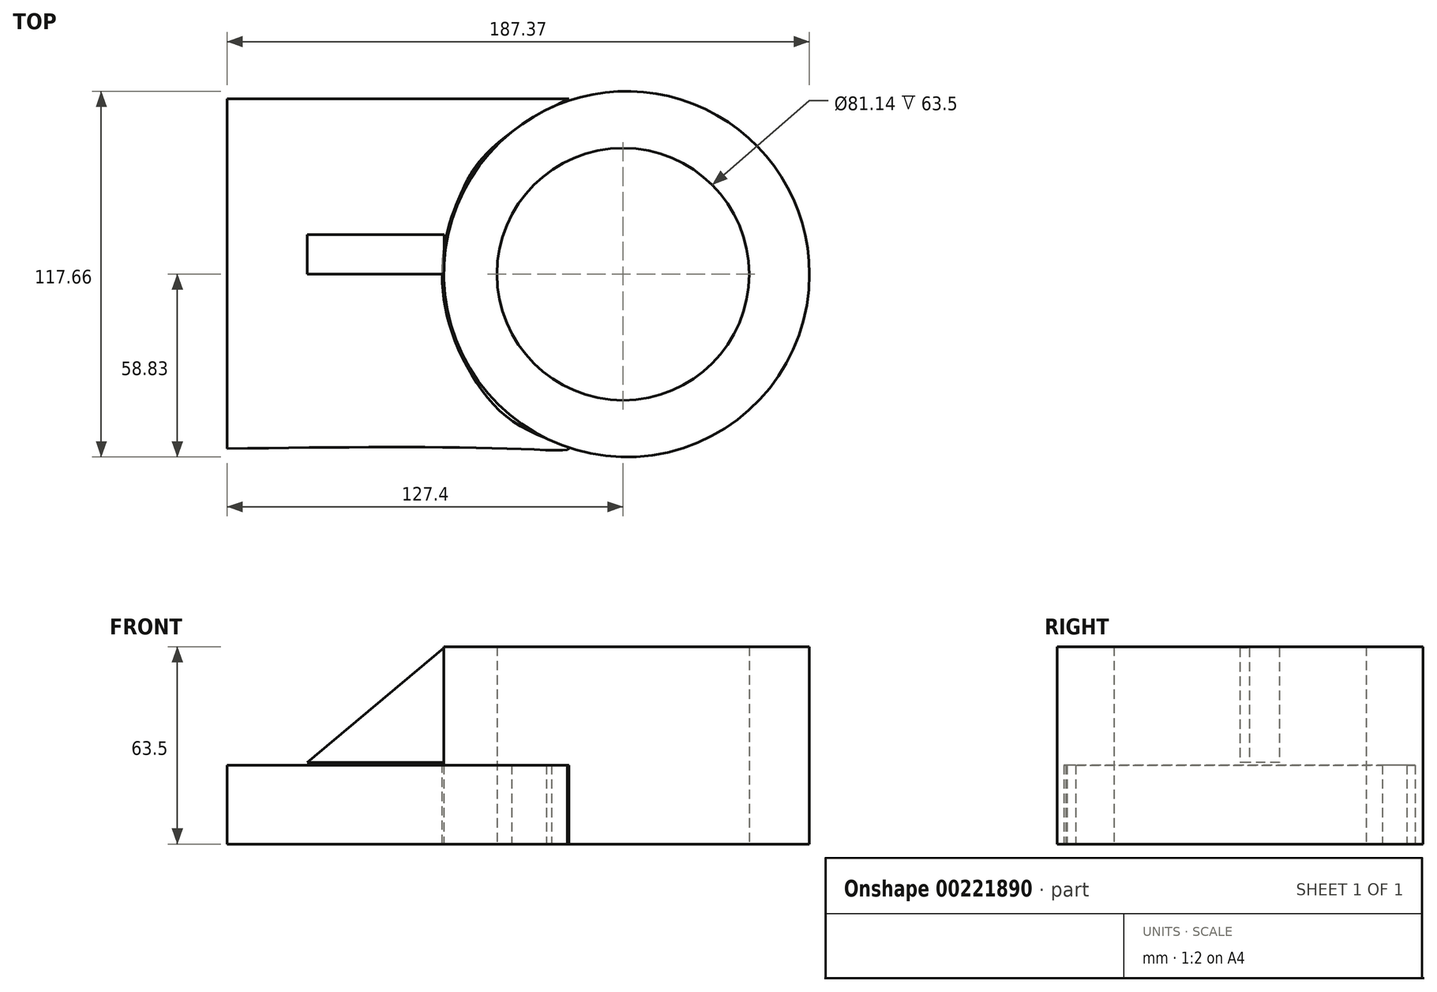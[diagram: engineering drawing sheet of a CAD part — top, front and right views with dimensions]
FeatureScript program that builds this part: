
annotation { "Feature Type Name" : "Feature", "Feature Type Description" : "" }
export const myFeature = defineFeature(function(context is Context, id is Id, definition is map)
    precondition{}
    {
        {
            var Q0;
            Q0=qCreatedBy(makeId("Top.planeOp"),FACE);
            var sketch = newSketch(context, id + "F0", { "sketchPlane" : qUnion([Q0])});
            skCircle(sketch, "E0", {"center": v(78.28, 0) * mm, "radius": 58.83 * mm});
            skSolve(sketch);
        }
        {
            var Q0;
            Q0 = qSketchRegion(id + "F0", true);
            extrude(context, id + "F1", {"entities" : qUnion([Q0]), "depth" : 63.5 * mm});
        }
        {
            var Q0;
            Q0=qCreatedBy(makeId("Top.planeOp"),FACE);
            var sketch = newSketch(context, id + "F2", { "sketchPlane" : qUnion([Q0])});
            skCircle(sketch, "E1", {"center": v(77.14, 0) * mm, "radius": 40.57 * mm});
            skSolve(sketch);
        }
        {
            var Q0;
            Q0 = qSketchRegion(id + "F2", true);
            extrude(context, id + "F3", {"entities" : qUnion([Q0]), "operationType" : NewBodyOperationType.REMOVE, "endBound" : BoundingType.THROUGH_ALL, "depth" : 101.6 * mm});
        }
        {
            var Q0;
            Q0=qCreatedBy(makeId("Top.planeOp"),FACE);
            var sketch = newSketch(context, id + "F4", { "sketchPlane" : qUnion([Q0])});
            skLineSegment(sketch, "E2", {"start": v(59.7, 56.39) * mm, "end": v(-50.26, 56.39) * mm});
            skLineSegment(sketch, "E3", {"start": v(-50.26, 56.39) * mm, "end": v(-50.26, -56.1) * mm});
            skFitSpline(sketch, "E4", {"points": [v(-50.26, -56.1) * mm, v(40.3, -56.1) * mm, v(59.7, -56.1) * mm, v(48.17, -51.04) * mm, v(33.83, -40.08) * mm, v(23.43, -22.36) * mm, v(19.2, -5.77) * mm, v(20.05, 11.39) * mm, v(25.4, 26.86) * mm, v(31.58, 36.98) * mm, v(45.64, 48.8) * mm, v(59.7, 56.39) * mm], "startDerivative": vector(530.88, 6.48) * mm, "endDerivative": vector(174.57, 84.25) * mm});
            skSolve(sketch);
        }
        {
            var Q0;
            Q0 = qSketchRegion(id + "F4", true);
            extrude(context, id + "F5", {"entities" : qUnion([Q0]), "operationType" : NewBodyOperationType.ADD, "depth" : 25.4 * mm});
        }
        {
            var Q0;
            Q0=qCreatedBy(makeId("Front.planeOp"),FACE);
            var sketch = newSketch(context, id + "F6", { "sketchPlane" : qUnion([Q0])});
            skLineSegment(sketch, "E5", {"start": v(19.52, 63.16) * mm, "end": v(19.52, 26.2) * mm});
            skLineSegment(sketch, "E6", {"start": v(19.52, 26.2) * mm, "end": v(-24.52, 26.2) * mm});
            skLineSegment(sketch, "E7", {"start": v(19.52, 63.16) * mm, "end": v(-24.52, 26.2) * mm});
            skSolve(sketch);
        }
        {
            var Q0;
            Q0 = qSketchRegion(id + "F6", true);
            extrude(context, id + "F7", {"entities" : qUnion([Q0]), "operationType" : NewBodyOperationType.ADD, "oppositeDirection" : true, "depth" : 12.7 * mm});
        }
    });
